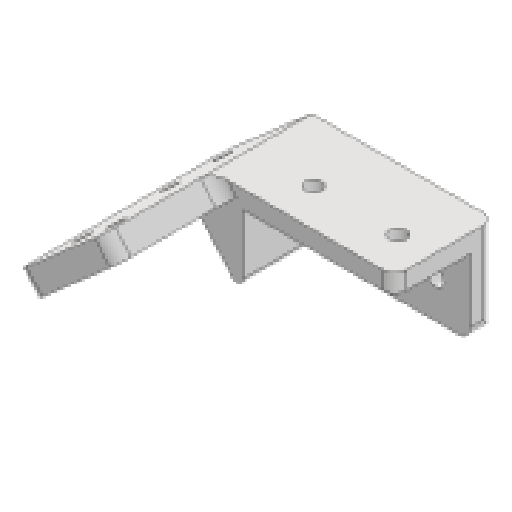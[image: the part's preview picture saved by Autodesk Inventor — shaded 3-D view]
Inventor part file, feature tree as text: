
AUTODESK INVENTOR PART (.ipt)
format: ipt  version: 2025 (Build 290162000, 162)  size: 181,760 bytes
history: native  units: mm
features: reference x7, extrude x5, sketch x5, other x5, projected_geometry x4, fillet x2
ambient origin geometry x8: Origin, YZ Plane, XZ Plane, XY Plane, X Axis, Y Axis, Z Axis, Center Point
bodies: Solid1 (feature_tree)
feature tree (28):
  extrude  "Extrusion1"  Depth=50.8mm
  extrude  "Extrusion2"  Depth=5.5mm
  extrude  "Extrusion3"  Depth=8.0mm TaperAngle=0.0deg
  extrude  "Extrusion4"  Depth=33.4mm
  extrude  "Extrusion5"  Depth=8.0mm TaperAngle=0.0deg
  fillet  "Fillet1"  [1 undecoded]
  fillet  "Fillet2"  Radius=2.0mm
  sketch  "Sketch1"  dims[d0=25.4mm d1=50.8mm]
  sketch  "Sketch2"  dims[d2=5.5mm d3=5.5mm]
  projected_geometry  "Projected Loop1"
  reference  "Reference1"
  sketch  "Sketch3"  dims[d4=25.4mm d5=8.0mm d6=0.0mm]
  reference  "Reference2"
  reference  "Reference3"
  projected_geometry  "Projected Loop2"
  reference  "Reference4"
  reference  "Reference5"
  reference  "Reference6"
  reference  "Reference7"
  sketch  "Sketch4"  dims[d7=33.4mm d8=0.0mm d9=5.5mm]
  projected_geometry  "Projected Loop3"
  sketch  "Sketch5"  dims[d10=8.0mm d11=0.0mm d12=8.0mm d13=0.0mm d14=0.0mm d15=0.0mm d16=2.0mm d17=4.0mm]
  projected_geometry  "Projected Loop4"
  other  "<userpath>\Desktop\puppycat\woodhouseMK1.iam"
  other  "woodhouseMK1.iam"
  other  "swingarmBaseV4:1"
  other  "horizontalStrut:1"
  other  "trackBase:1"
note: 1 required parameter value undecoded (feature->parameter linkage not recoverable at this tier; creation-order binding heuristic only, values carry confidence <= 0.55)
